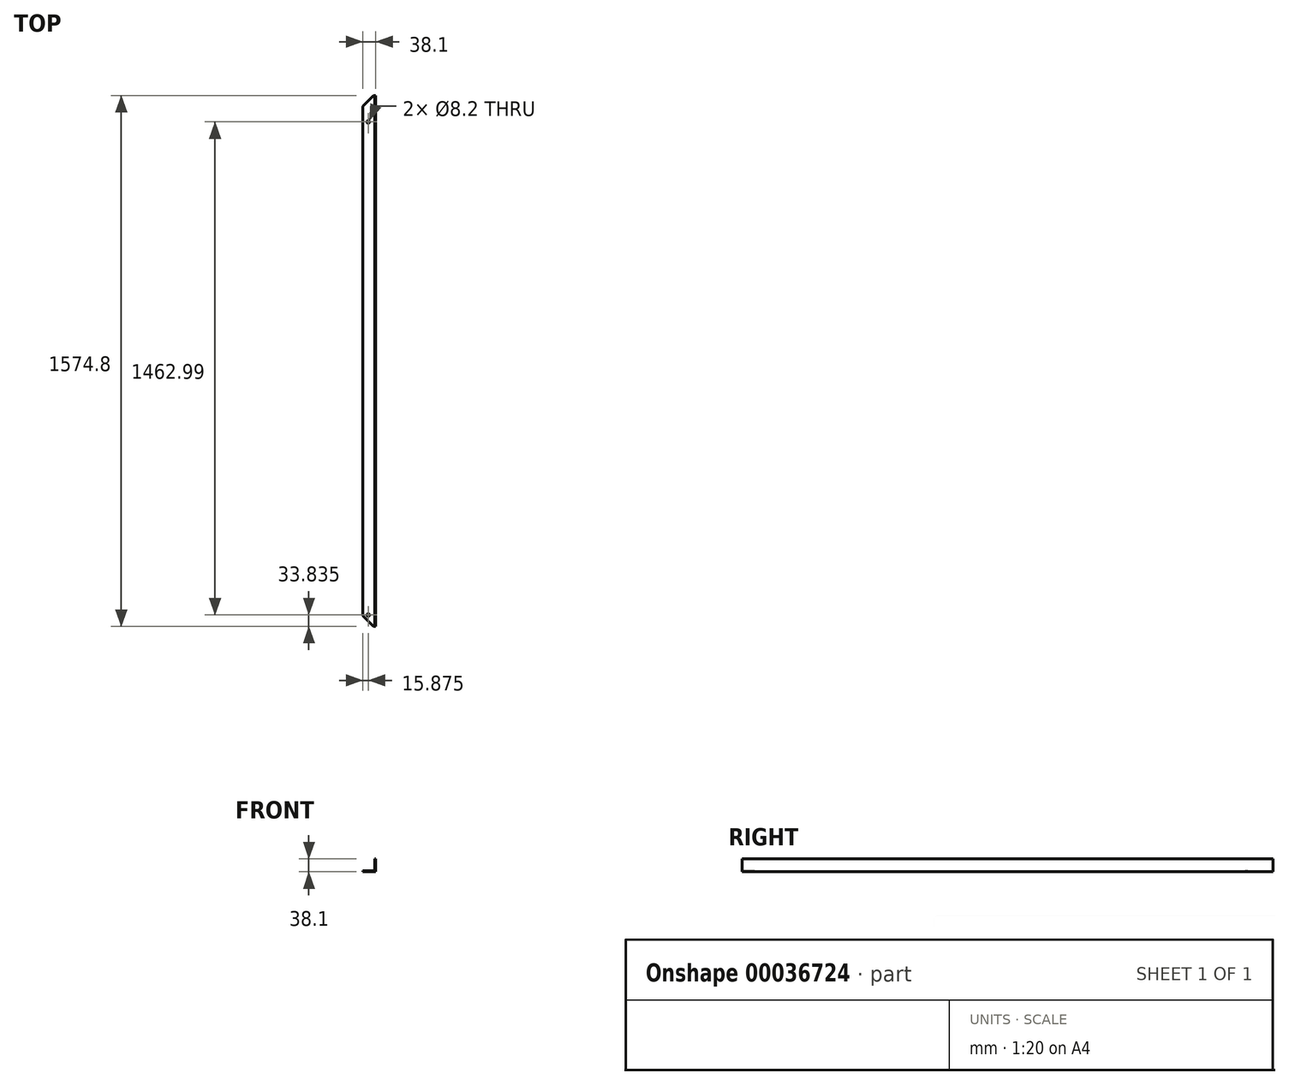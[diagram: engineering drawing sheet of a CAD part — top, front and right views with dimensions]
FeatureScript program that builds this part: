
annotation { "Feature Type Name" : "Feature", "Feature Type Description" : "" }
export const myFeature = defineFeature(function(context is Context, id is Id, definition is map)
    precondition{}
    {
        {
            var Q0;
            Q0=qCreatedBy(makeId("Front.planeOp"),FACE);
            var sketch = newSketch(context, id + "F0", { "sketchPlane" : qUnion([Q0])});
            skLineSegment(sketch, "E0", {"start": v(0, 0) * mm, "end": v(38.1, 0) * mm});
            skLineSegment(sketch, "E1", {"start": v(38.1, 0) * mm, "end": v(38.1, 38.1) * mm});
            skLineSegment(sketch, "E2", {"start": v(38.1, 38.1) * mm, "end": v(34.93, 38.1) * mm});
            skLineSegment(sketch, "E3", {"start": v(34.93, 38.1) * mm, "end": v(34.93, 3.18) * mm});
            skLineSegment(sketch, "E4", {"start": v(34.93, 3.18) * mm, "end": v(0, 3.18) * mm});
            skLineSegment(sketch, "E5", {"start": v(0, 3.18) * mm, "end": v(0, 0) * mm});
            skSolve(sketch);
        }
        {
            var Q0;
            Q0=makeQuery(id+"F0.imprint","IMPRINT",FACE,{"disambiguationData":[TD([[makeQuery(id+"F0.imprint","IMPRINT",EDGE,{"derivedFrom":sQuery(id+"F0.wireOp",EDGE,"E0")}),1.0]])]});
            extrude(context, id + "F1", {"entities" : qUnion([Q0]), "depth" : 1574.8 * mm, "offsetDistance" : 25.4 * mm});
        }
        {
            var Q0;
            Q0=makeQuery(id+"F1.opExtrude","SWEPT_FACE",FACE,{"disambiguationData":[OSD([sQuery(id+"F0.wireOp",EDGE,"E4")])]});
            var sketch = newSketch(context, id + "F2", { "sketchPlane" : qUnion([Q0])});
            skLineSegment(sketch, "E6", {"start": v(31.75, -1574.8) * mm, "end": v(0, -1574.8) * mm});
            skLineSegment(sketch, "E7", {"start": v(0, -1574.8) * mm, "end": v(0, -1543.05) * mm});
            skLineSegment(sketch, "E8", {"start": v(0, -1543.05) * mm, "end": v(31.75, -1574.8) * mm});
            skLineSegment(sketch, "E9", {"start": v(0, -31.75) * mm, "end": v(0, 0) * mm});
            skLineSegment(sketch, "E10", {"start": v(0, -31.75) * mm, "end": v(31.75, 0) * mm});
            skLineSegment(sketch, "E11", {"start": v(31.75, 0) * mm, "end": v(0, 0) * mm});
            skSolve(sketch);
        }
        {
            var Q0;
            Q0=makeQuery(id+"F2.imprint","IMPRINT",FACE,{"disambiguationData":[TD([[makeQuery(id+"F2.imprint","IMPRINT",EDGE,{"derivedFrom":sQuery(id+"F2.wireOp",EDGE,"E6")}),-1.0]])]});
            var Q1;
            Q1=makeQuery(id+"F2.imprint","IMPRINT",FACE,{"disambiguationData":[TD([[makeQuery(id+"F2.imprint","IMPRINT",EDGE,{"derivedFrom":sQuery(id+"F2.wireOp",EDGE,"E9")}),-1.0]])]});
            extrude(context, id + "F3", {"entities" : qUnion([Q0, Q1]), "operationType" : NewBodyOperationType.REMOVE, "endBound" : BoundingType.THROUGH_ALL, "oppositeDirection" : true, "depth" : 25.4 * mm, "offsetDistance" : 25.4 * mm});
        }
        {
            var Q0;
            Q0=makeQuery(id+"F1.opExtrude","SWEPT_FACE",FACE,{"disambiguationData":[OSD([sQuery(id+"F0.wireOp",EDGE,"E4")])]});
            var sketch = newSketch(context, id + "F4", { "sketchPlane" : qUnion([Q0])});
            skPoint(sketch, "E12", {"position": v(15.88, -1540.96) * mm});
            skPoint(sketch, "E13", {"position": v(15.88, -77.98) * mm});
            skSolve(sketch);
        }
        {
            var Q0;
            Q0=sQuery(id+"F4.wireOp",VERTEX,"E12");
            var Q1;
            Q1=sQuery(id+"F4.wireOp",VERTEX,"E13");
            var Q2;
            Q2=makeQuery(id+"F1.opExtrude","SWEPT_BODY",BODY,{"disambiguationData":[OSD([sQuery(id+"F0.wireOp",EDGE,"E0"),sQuery(id+"F0.wireOp",EDGE,"E1"),sQuery(id+"F0.wireOp",EDGE,"E2"),sQuery(id+"F0.wireOp",EDGE,"E3"),sQuery(id+"F0.wireOp",EDGE,"E4"),sQuery(id+"F0.wireOp",EDGE,"E5")])]});
            hole(context, id + "F5", {"style" : HoleStyle.SIMPLE, "endStyle" : HoleEndStyle.THROUGH, "standardTappedOrClearance" : lookupTablePath({ "standard" : "ANSI", "fit" : "Close", "size" : "5/16", "type" : "Clearance" }), "standardBlindInLast" : lookupTablePath({ "fit" : "Close", "standard" : "ANSI", "size" : "5/16", "type" : "Clearance" }), "holeDiameter" : 8.2 * mm, "majorDiameter" : 6.35 * mm, "tappedDepth" : 6.35 * mm, "tapClearance" : 3, "locations" : qUnion([Q0, Q1]), "scope" : qUnion([Q2])});
        }
    });
